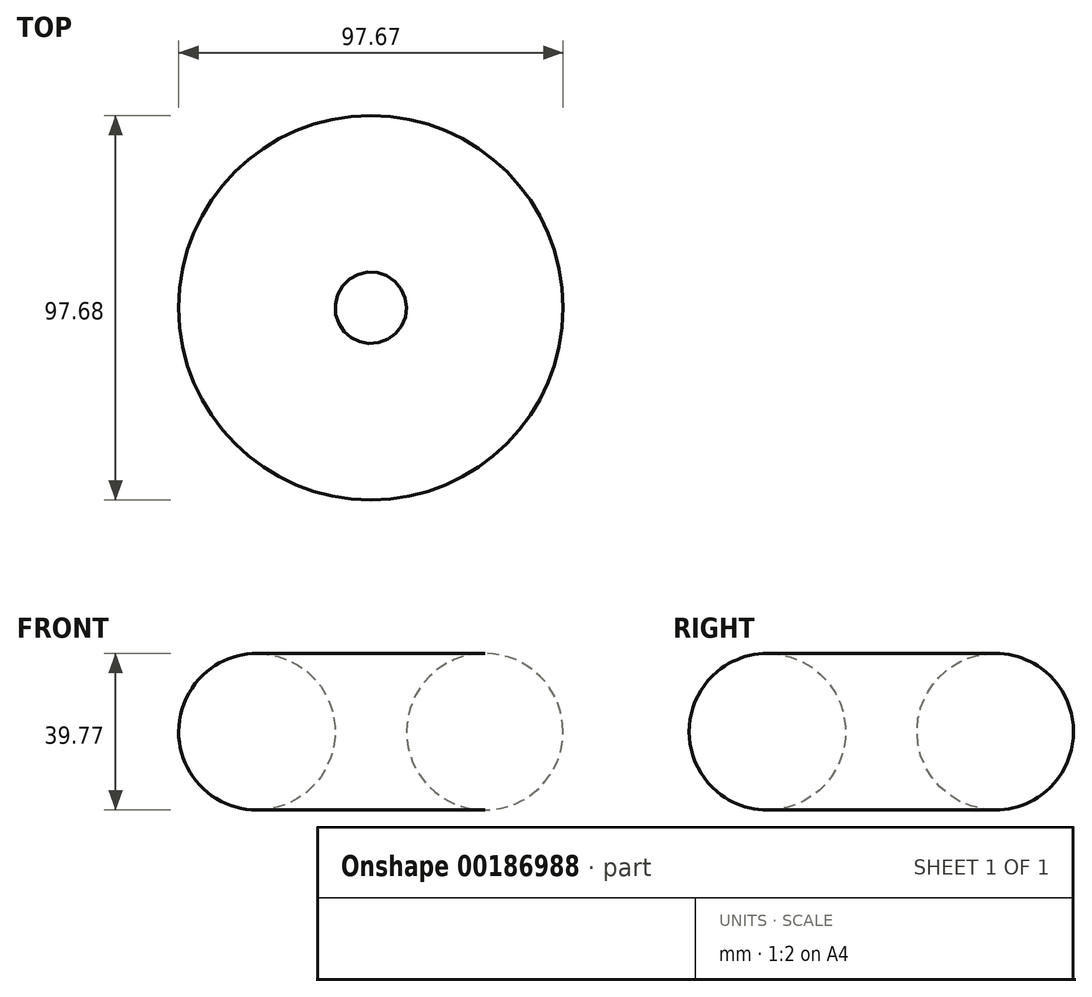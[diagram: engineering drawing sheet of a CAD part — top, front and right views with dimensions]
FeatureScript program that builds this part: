
annotation { "Feature Type Name" : "Feature", "Feature Type Description" : "" }
export const myFeature = defineFeature(function(context is Context, id is Id, definition is map)
    precondition{}
    {
        {
            var Q0;
            Q0=qCreatedBy(makeId("Front.planeOp"),FACE);
            var sketch = newSketch(context, id + "F0", { "sketchPlane" : qUnion([Q0])});
            skCircle(sketch, "E0", {"center": v(-45.32, 31.55) * mm, "radius": 19.88 * mm});
            skLineSegment(sketch, "E1", {"start": v(-16.37, 40.13) * mm, "end": v(-16.37, 29.1) * mm});
            skSolve(sketch);
        }
        {
            var Q0;
            Q0=makeQuery(id+"F0.imprint","IMPRINT",FACE,{"disambiguationData":[TD([[makeQuery(id+"F0.imprint","IMPRINT",EDGE,{"derivedFrom":sQuery(id+"F0.wireOp",EDGE,"E0")}),1.0]])]});
            var Q1;
            Q1=sQuery(id+"F0.wireOp",EDGE,"E1");
            var Q2;
            Q2=sQuery(id+"F0.wireOp",EDGE,"E1");
            revolve(context, id + "F1", {"entities" : qUnion([Q0]), "axis" : qUnion([Q1, Q2]), "revolveType" : RevolveType.FULL});
        }
    });
